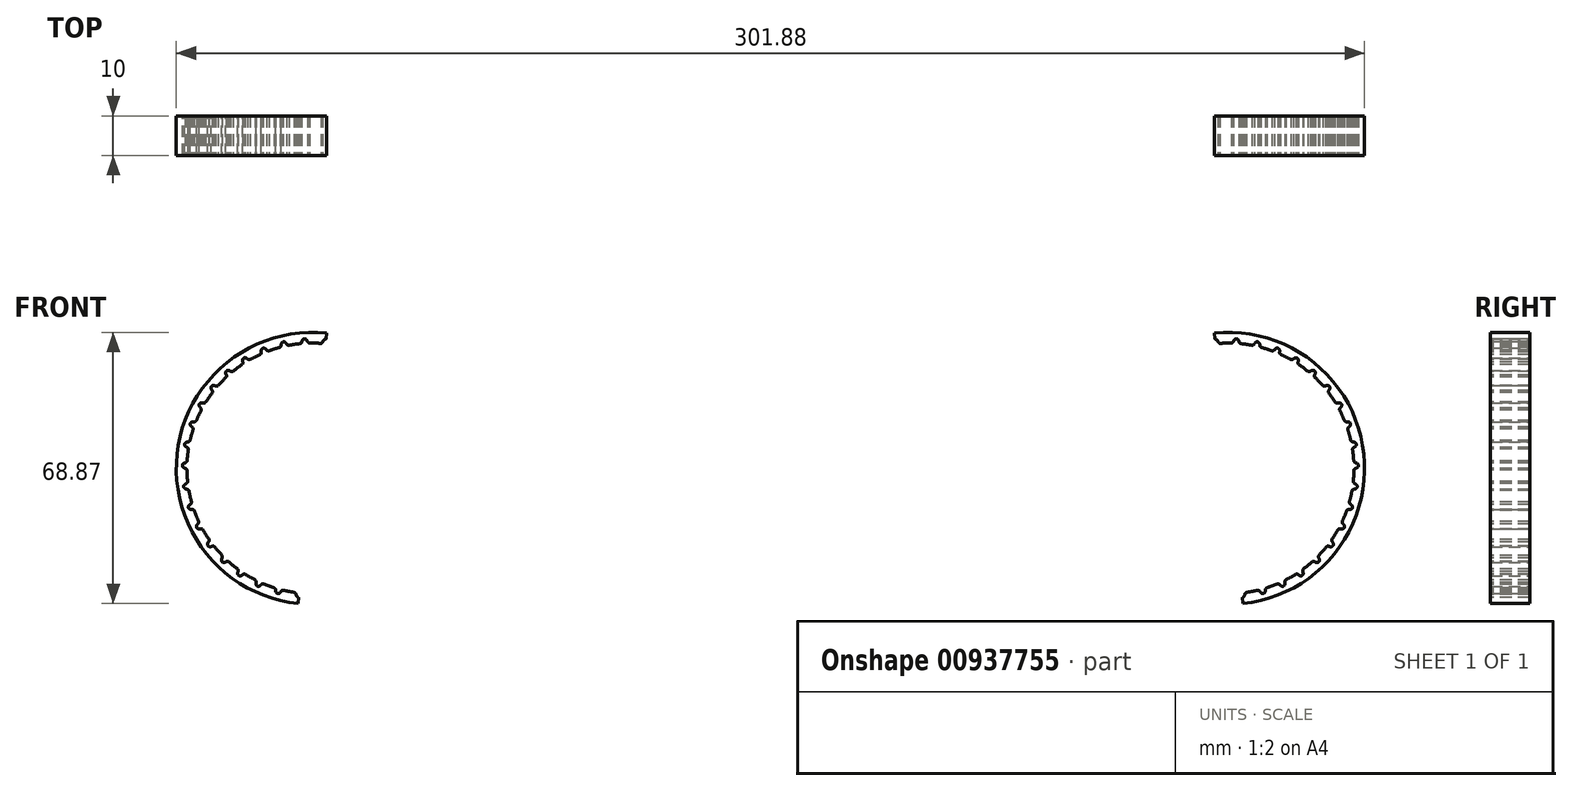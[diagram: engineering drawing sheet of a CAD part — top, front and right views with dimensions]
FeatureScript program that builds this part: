
annotation { "Feature Type Name" : "Feature", "Feature Type Description" : "" }
export const myFeature = defineFeature(function(context is Context, id is Id, definition is map)
    precondition{}
    {
        {
            var Q0;
            Q0=qCreatedBy(makeId("Front.planeOp"),FACE);
            var sketch = newSketch(context, id + "F0", { "sketchPlane" : qUnion([Q0])});
            skArc(sketch, "E0", {"start": v(120.96, -47.24) * mm, "mid": v(122.42, -47) * mm, "end": v(123.87, -46.68) * mm});
            skArc(sketch, "E1", {"start": v(120.05, -50.07) * mm, "mid": v(150.75, -12.1) * mm, "end": v(112.77, 18.6) * mm});
            skEllipticalArc(sketch, "E2.5.0.0", {});
            skArc(sketch, "E2.5.0.1", {"start": v(113.73, 16.4) * mm, "mid": v(113.93, 16.15) * mm, "end": v(114.2, 16) * mm});
            skEllipticalArc(sketch, "E2.5.0.3", {});
            skEllipticalArc(sketch, "E3.1.0", {});
            skArc(sketch, "E3.1.1", {"start": v(119.06, 16.4) * mm, "mid": v(119.2, 16.12) * mm, "end": v(119.46, 15.93) * mm});
            skEllipticalArc(sketch, "E3.2.0", {});
            skArc(sketch, "E3.2.1", {"start": v(124.31, 15.53) * mm, "mid": v(124.41, 15.23) * mm, "end": v(124.63, 15) * mm});
            skEllipticalArc(sketch, "E3.3.0", {});
            skArc(sketch, "E3.3.1", {"start": v(129.35, 13.8) * mm, "mid": v(129.4, 13.49) * mm, "end": v(129.57, 13.23) * mm});
            skEllipticalArc(sketch, "E3.4.0", {});
            skArc(sketch, "E3.4.1", {"start": v(134.04, 11.27) * mm, "mid": v(134.03, 10.95) * mm, "end": v(134.16, 10.67) * mm});
            skEllipticalArc(sketch, "E3.5.0", {});
            skArc(sketch, "E3.5.1", {"start": v(138.24, 8) * mm, "mid": v(138.19, 7.69) * mm, "end": v(138.26, 7.38) * mm});
            skEllipticalArc(sketch, "E3.6.0", {});
            skArc(sketch, "E3.6.1", {"start": v(141.85, 4.08) * mm, "mid": v(141.74, 3.79) * mm, "end": v(141.77, 3.47) * mm});
            skEllipticalArc(sketch, "E3.7.0", {});
            skArc(sketch, "E3.7.1", {"start": v(144.76, -0.37) * mm, "mid": v(144.61, -0.65) * mm, "end": v(144.59, -0.96) * mm});
            skEllipticalArc(sketch, "E3.8.0", {});
            skArc(sketch, "E3.8.1", {"start": v(146.9, -5.25) * mm, "mid": v(146.7, -5.5) * mm, "end": v(146.63, -5.8) * mm});
            skEllipticalArc(sketch, "E3.9.0", {});
            skArc(sketch, "E3.9.1", {"start": v(148.22, -10.41) * mm, "mid": v(147.98, -10.62) * mm, "end": v(147.86, -10.91) * mm});
            skEllipticalArc(sketch, "E3.10.0", {});
            skArc(sketch, "E3.10.1", {"start": v(148.66, -15.72) * mm, "mid": v(148.4, -15.89) * mm, "end": v(148.22, -16.15) * mm});
            skEllipticalArc(sketch, "E3.11.0", {});
            skArc(sketch, "E3.11.1", {"start": v(148.22, -21.03) * mm, "mid": v(147.93, -21.15) * mm, "end": v(147.72, -21.38) * mm});
            skEllipticalArc(sketch, "E3.12.0", {});
            skArc(sketch, "E3.12.1", {"start": v(146.92, -26.19) * mm, "mid": v(146.6, -26.26) * mm, "end": v(146.36, -26.46) * mm});
            skEllipticalArc(sketch, "E3.13.0", {});
            skArc(sketch, "E3.13.1", {"start": v(144.78, -31.07) * mm, "mid": v(144.46, -31.1) * mm, "end": v(144.19, -31.24) * mm});
            skEllipticalArc(sketch, "E3.14.0", {});
            skArc(sketch, "E3.14.1", {"start": v(141.87, -35.53) * mm, "mid": v(141.55, -35.5) * mm, "end": v(141.26, -35.6) * mm});
            skEllipticalArc(sketch, "E3.15.0", {});
            skArc(sketch, "E3.15.1", {"start": v(138.26, -39.45) * mm, "mid": v(137.96, -39.37) * mm, "end": v(137.65, -39.42) * mm});
            skEllipticalArc(sketch, "E3.16.0", {});
            skArc(sketch, "E3.16.1", {"start": v(134.06, -42.72) * mm, "mid": v(133.77, -42.6) * mm, "end": v(133.46, -42.6) * mm});
            skEllipticalArc(sketch, "E3.17.0", {});
            skArc(sketch, "E3.17.1", {"start": v(129.38, -45.26) * mm, "mid": v(129.12, -45.08) * mm, "end": v(128.8, -45.03) * mm});
            skEllipticalArc(sketch, "E3.18.0", {});
            skArc(sketch, "E3.18.1", {"start": v(124.34, -46.99) * mm, "mid": v(124.11, -46.77) * mm, "end": v(123.82, -46.67) * mm});
            skLineSegment(sketch, "E3.anchor1", {"start": v(116.41, -15.73) * mm, "end": v(113.03, 16.09) * mm, "construction": true});
            skArc(sketch, "E4.1.0", {"start": v(117.11, 16.09) * mm, "mid": v(117.42, 16.23) * mm, "end": v(117.64, 16.5) * mm});
            skEllipticalArc(sketch, "E4.1.1", {});
            skArc(sketch, "E4.2.0", {"start": v(122.34, 15.54) * mm, "mid": v(122.67, 15.63) * mm, "end": v(122.93, 15.86) * mm});
            skEllipticalArc(sketch, "E4.2.1", {});
            skArc(sketch, "E4.3.0", {"start": v(127.4, 14.14) * mm, "mid": v(127.75, 14.17) * mm, "end": v(128.04, 14.35) * mm});
            skEllipticalArc(sketch, "E4.3.1", {});
            skArc(sketch, "E4.4.0", {"start": v(132.17, 11.92) * mm, "mid": v(132.52, 11.9) * mm, "end": v(132.83, 12.03) * mm});
            skEllipticalArc(sketch, "E4.4.1", {});
            skArc(sketch, "E4.5.0", {"start": v(136.51, 8.95) * mm, "mid": v(136.84, 8.87) * mm, "end": v(137.18, 8.95) * mm});
            skEllipticalArc(sketch, "E4.5.1", {});
            skArc(sketch, "E4.6.0", {"start": v(140.3, 5.3) * mm, "mid": v(140.62, 5.17) * mm, "end": v(140.96, 5.2) * mm});
            skEllipticalArc(sketch, "E4.6.1", {});
            skArc(sketch, "E4.7.0", {"start": v(143.44, 1.08) * mm, "mid": v(143.73, 0.9) * mm, "end": v(144.07, 0.87) * mm});
            skEllipticalArc(sketch, "E4.7.1", {});
            skArc(sketch, "E4.8.0", {"start": v(145.84, -3.6) * mm, "mid": v(146.1, -3.82) * mm, "end": v(146.42, -3.9) * mm});
            skEllipticalArc(sketch, "E4.8.1", {});
            skArc(sketch, "E4.9.0", {"start": v(147.43, -8.6) * mm, "mid": v(147.65, -8.87) * mm, "end": v(147.96, -9) * mm});
            skEllipticalArc(sketch, "E4.9.1", {});
            skArc(sketch, "E4.10.0", {"start": v(148.18, -13.8) * mm, "mid": v(148.35, -14.1) * mm, "end": v(148.64, -14.3) * mm});
            skEllipticalArc(sketch, "E4.10.1", {});
            skArc(sketch, "E4.11.0", {"start": v(148.07, -19.06) * mm, "mid": v(148.19, -19.38) * mm, "end": v(148.43, -19.62) * mm});
            skEllipticalArc(sketch, "E4.11.1", {});
            skArc(sketch, "E4.12.0", {"start": v(147.09, -24.22) * mm, "mid": v(147.15, -24.56) * mm, "end": v(147.36, -24.83) * mm});
            skEllipticalArc(sketch, "E4.12.1", {});
            skArc(sketch, "E4.13.0", {"start": v(145.27, -29.16) * mm, "mid": v(145.28, -29.5) * mm, "end": v(145.44, -29.8) * mm});
            skEllipticalArc(sketch, "E4.13.1", {});
            skArc(sketch, "E4.14.0", {"start": v(142.67, -33.73) * mm, "mid": v(142.62, -34.06) * mm, "end": v(142.73, -34.39) * mm});
            skEllipticalArc(sketch, "E4.14.1", {});
            skArc(sketch, "E4.15.0", {"start": v(139.35, -37.8) * mm, "mid": v(139.25, -38.13) * mm, "end": v(139.3, -38.47) * mm});
            skEllipticalArc(sketch, "E4.15.1", {});
            skArc(sketch, "E4.16.0", {"start": v(135.4, -41.28) * mm, "mid": v(135.25, -41.58) * mm, "end": v(135.24, -41.92) * mm});
            skEllipticalArc(sketch, "E4.16.1", {});
            skArc(sketch, "E4.17.0", {"start": v(130.94, -44.05) * mm, "mid": v(130.74, -44.33) * mm, "end": v(130.68, -44.66) * mm});
            skEllipticalArc(sketch, "E4.17.1", {});
            skArc(sketch, "E4.18.0", {"start": v(126.08, -46.06) * mm, "mid": v(125.84, -46.3) * mm, "end": v(125.72, -46.62) * mm});
            skEllipticalArc(sketch, "E4.18.1", {});
            skArc(sketch, "E4.19.0", {"start": v(120.96, -47.24) * mm, "mid": v(120.68, -47.43) * mm, "end": v(120.5, -47.73) * mm});
            skEllipticalArc(sketch, "E4.19.1", {});
            skLineSegment(sketch, "E4.anchor2", {"start": v(116.41, -15.73) * mm, "end": v(120.96, -47.24) * mm, "construction": true});
            skPoint(sketch, "E5.orphan", {"position": v(119.1, -47.87) * mm});
            skLineSegment(sketch, "E6", {"start": v(119.8, -47.55) * mm, "end": v(119.77, -47.39) * mm});
            skLineSegment(sketch, "E7", {"start": v(119.89, -48.55) * mm, "end": v(120.05, -50.07) * mm});
            skLineSegment(sketch, "E8", {"start": v(120.05, -50.07) * mm, "end": v(120.06, -50.05) * mm});
            skLineSegment(sketch, "E9", {"start": v(113.05, 15.92) * mm, "end": v(113.03, 16.09) * mm});
            skArc(sketch, "E10.trimOffspring", {"start": v(117.11, 16.09) * mm, "mid": v(115.63, 16.09) * mm, "end": v(114.15, 16.02) * mm});
            skArc(sketch, "E11.trimOffspring", {"start": v(122.34, 15.54) * mm, "mid": v(120.88, 15.78) * mm, "end": v(119.41, 15.95) * mm});
            skArc(sketch, "E12.trimOffspring", {"start": v(127.4, 14.14) * mm, "mid": v(126, 14.62) * mm, "end": v(124.59, 15.03) * mm});
            skArc(sketch, "E13.trimOffspring", {"start": v(132.17, 11.92) * mm, "mid": v(130.87, 12.62) * mm, "end": v(129.54, 13.26) * mm});
            skArc(sketch, "E14.trimOffspring", {"start": v(136.51, 8.95) * mm, "mid": v(135.34, 9.86) * mm, "end": v(134.13, 10.7) * mm});
            skArc(sketch, "E15.trimOffspring", {"start": v(140.3, 5.3) * mm, "mid": v(139.3, 6.4) * mm, "end": v(138.24, 7.43) * mm});
            skArc(sketch, "E16.trimOffspring", {"start": v(143.44, 1.08) * mm, "mid": v(142.63, 2.32) * mm, "end": v(141.76, 3.52) * mm});
            skArc(sketch, "E17.trimOffspring", {"start": v(145.84, -3.6) * mm, "mid": v(145.24, -2.24) * mm, "end": v(144.58, -0.91) * mm});
            skArc(sketch, "E18.trimOffspring", {"start": v(147.43, -8.6) * mm, "mid": v(147.07, -7.17) * mm, "end": v(146.64, -5.75) * mm});
            skArc(sketch, "E19.trimOffspring", {"start": v(148.18, -13.8) * mm, "mid": v(148.06, -12.33) * mm, "end": v(147.87, -10.86) * mm});
            skArc(sketch, "E20.trimOffspring", {"start": v(148.07, -19.06) * mm, "mid": v(148.19, -17.58) * mm, "end": v(148.24, -16.1) * mm});
            skArc(sketch, "E21.trimOffspring", {"start": v(147.09, -24.22) * mm, "mid": v(147.45, -22.79) * mm, "end": v(147.75, -21.34) * mm});
            skArc(sketch, "E22.trimOffspring", {"start": v(145.27, -29.16) * mm, "mid": v(145.87, -27.8) * mm, "end": v(146.4, -26.42) * mm});
            skArc(sketch, "E23.trimOffspring", {"start": v(142.67, -33.73) * mm, "mid": v(143.48, -32.49) * mm, "end": v(144.23, -31.2) * mm});
            skArc(sketch, "E24.trimOffspring", {"start": v(139.35, -37.8) * mm, "mid": v(140.35, -36.71) * mm, "end": v(141.3, -35.58) * mm});
            skArc(sketch, "E25.trimOffspring", {"start": v(135.4, -41.28) * mm, "mid": v(136.57, -40.37) * mm, "end": v(137.7, -39.4) * mm});
            skArc(sketch, "E26.trimOffspring", {"start": v(130.94, -44.05) * mm, "mid": v(132.24, -43.35) * mm, "end": v(133.51, -42.58) * mm});
            skArc(sketch, "E27.trimOffspring", {"start": v(126.08, -46.06) * mm, "mid": v(127.48, -45.58) * mm, "end": v(128.86, -45.03) * mm});
            skLineSegment(sketch, "E28.trimOffspring", {"start": v(112.93, 17.08) * mm, "end": v(112.77, 18.6) * mm});
            const initialGuessF0  = {"E2.5.0.0": [0.11303482814067517, 0.016085284111386752, -0.09793029370573542, 0.9951932764919127, 0.001, 0.0007199110732306023, 0, 0.010662289715557305], "E2.5.0.3": [0.11303482814067461, 0.016085284111387186, -0.09793029370571554, 0.9951932764919146, 0.001, 0.00075, 4.958959793330978, 6.283185307179577], "E3.1.0": [0.11831822491139382, 0.01620729971119933, 0.06720877745214683, 0.997738933906755, 0.001, 0.00075, 4.958959793330976, 0], "E3.2.0": [0.12354964614421307, 0.01545803265049844, 0.23051456836132156, 0.9730688741159045, 0.001, 0.00075, 4.958959793330976, 0], "E3.3.0": [0.12858639230519847, 0.013857920981506955, 0.38753252275223143, 0.921856032040411, 0.001, 0.00075, 4.958959793330976, 0], "E3.4.0": [0.13329107408889557, 0.011450611579375158, 0.5339796001443508, 0.8454973605101789, 0.001, 0.00075, 4.958959793330976, 0], "E3.5.0": [0.13753536004043526, 0.008301769569205947, 0.6658611060254611, 0.746075725032352, 0.001, 0.00075, 4.958959793330976, 0], "E3.6.0": [0.14120347710308728, 0.00449728715261824, 0.7795796567045535, 0.6263030886499048, 0.001, 0.00075, 4.958959793330976, 0], "E3.7.0": [0.14419536860544996, 0.00014094069239109497, 0.8720333065612396, 0.4894465366593897, 0.001, 0.00075, 4.958959793330976, 0], "E3.8.0": [0.14642942354661792, -0.004648440036188195, 0.9407001610361064, 0.3392391590407031, 0.001, 0.00075, 4.958959793330976, 0], "E3.9.0": [0.14784470273154268, -0.00974021321182772, 0.98370716734021, 0.179778221493873, 0.001, 0.00075, 4.958959793330976, 0], "E3.10.0": [0.14840260103341701, -0.014995488535558099, 0.9998812064524727, 0.0154134027115367, 0.001, 0.00075, 4.958959793330976, 0], "E3.11.0": [0.1480879004408981, -0.02027091579602827, 0.9887810927484848, -0.14937185351702803, 0.001, 0.00075, 4.958959793330976, 0], "E3.12.0": [0.14690918516578663, -0.025422595089585068, 0.9507096083942551, -0.3100826349650073, 0.001, 0.00075, 4.9589597933309575, 6.283185307179583], "E3.13.0": [0.14489860748810623, -0.030310002034525982, 0.8867052442380137, -0.46233517045624434, 0.001, 0.00075, 4.958959793330978, 6.283185307179582], "E3.14.0": [0.14211101072571924, -0.034799820909912065, 0.7985138724870178, -0.6019764077152749, 0.001, 0.00075, 4.958959793330948, 0], "E3.15.0": [0.13862243325158113, -0.03876958116090705, 0.6885411238648864, -0.72519729780721, 0.001, 0.00075, 4.9589597933309735, 6.283185307179575], "E3.16.0": [0.1345280343651436, -0.04211099807625639, 0.5597867682764718, -0.8286366960632288, 0.001, 0.00075, 4.958959793330938, 0], "E3.17.0": [0.12993949859472742, -0.044732926512933195, 0.4157628889046707, -0.9094730453452936, 0.001, 0.00075, 4.958959793330925, 6.283185307179573], "E3.18.0": [0.12498198923472943, -0.046563847098042246, 0.26039808173651235, -0.9655013407696256, 0.001, 0.00075, 4.958959793330958, 0], "E4.1.1": [0.11831822491139428, 0.016207299711198813, 0.0672087774521269, 0.9977389339067563, 0.001, 0.0007199110732306023, 0, 1.3242255138486463], "E4.2.1": [0.12354964614421346, 0.015458032650497847, 0.23051456836130213, 0.973068874115909, 0.001, 0.0007199110732306023, 0, 1.3242255138486463], "E4.3.1": [0.12858639230519875, 0.01385792098150631, 0.38753252275221306, 0.9218560320404188, 0.001, 0.0007199110732306023, 0, 1.3242255138486463], "E4.4.1": [0.13329107408889576, 0.011450611579374478, 0.5339796001443338, 0.8454973605101896, 0.001, 0.0007199110732306023, 0, 1.3242255138486463], "E4.5.1": [0.13753536004043532, 0.008301769569205253, 0.6658611060254462, 0.7460757250323654, 0.001, 0.0007199110732306023, 0, 1.3242255138486463], "E4.6.1": [0.14120347710308723, 0.004497287152617546, 0.7795796567045411, 0.6263030886499203, 0.001, 0.0007199110732306023, 0, 1.3242255138486463], "E4.7.1": [0.1441953686054498, 0.00014094069239041496, 0.8720333065612298, 0.4894465366594071, 0.001, 0.0007199110732306023, 0, 1.3242255138486463], "E4.8.1": [0.14642942354661762, -0.004648440036188847, 0.9407001610360997, 0.33923915904072194, 0.001, 0.0007199110732306023, 0, 1.3242255138486463], "E4.9.1": [0.1478447027315423, -0.009740213211828302, 0.9837071673402066, 0.17977822149389266, 0.001, 0.0007199110732306023, 0, 1.3242255138486463], "E4.10.1": [0.14840260103341651, -0.014995488535558626, 0.9998812064524724, 0.015413402711556654, 0.001, 0.0007199110732306023, 0, 1.3242255138486463], "E4.11.1": [0.14808790044089754, -0.020270915796028702, 0.9887810927484878, -0.14937185351700832, 0.001, 0.0007199110732306023, 0, 1.3242255138486463], "E4.12.1": [0.146909185165786, -0.02542259508958547, 0.9507096083942608, -0.3100826349649908, 0.001, 0.0007199110732306023, 0, 1.3242255138486463], "E4.13.1": [0.14489860748810554, -0.030310002034526315, 0.8867052442380217, -0.46233517045622935, 0.001, 0.0007199110732306023, 0, 1.3242255138486463], "E4.14.1": [0.1421110107257185, -0.03479982090991225, 0.7985138724870282, -0.6019764077152611, 0.001, 0.0007199110732306023, 0, 1.3242255138486463], "E4.15.1": [0.13862243325158036, -0.0387695811609071, 0.6885411238648989, -0.7251972978071982, 0.001, 0.0007199110732306023, 0, 1.3242255138486463], "E4.16.1": [0.13452803436514282, -0.042110998076256324, 0.5597867682764859, -0.8286366960632193, 0.001, 0.0007199110732306023, 0, 1.3242255138486463], "E4.17.1": [0.1299394985947266, -0.04473292651293303, 0.41576288890468527, -0.9094730453452871, 0.001, 0.0007199110732306023, 0, 1.3242255138486463], "E4.18.1": [0.1249819892347287, -0.04656384709804196, 0.26039808173652823, -0.9655013407696214, 0.001, 0.0007199110732306023, 0, 1.3242255138486463], "E4.19.1": [0.11979073421722736, -0.047553817090875125, 0.09793029370573554, -0.9951932764919127, 0.001, 0.0007199110732306023, 0, 1.3242255138486463]};
            skSetInitialGuess(sketch, initialGuessF0);
            skSolve(sketch);
        }
        {
            var Q0;
            {var subQ2=sQuery(id+"F0.wireOp",EDGE,"E3.6.0");Q0=makeQuery(id+"F0.imprint","IMPRINT",FACE,{"disambiguationData":[TD([[makeQuery(id+"F0.imprint","IMPRINT",EDGE,{"derivedFrom":subQ2}),1.0]])]});}
            var Q1;
            {var subQ44=sQuery(id+"F0.wireOp",EDGE,"E1");Q1=makeQuery(id+"F0.imprint","IMPRINT",FACE,{"disambiguationData":[TD([[makeQuery(id+"F0.imprint","IMPRINT",EDGE,{"derivedFrom":subQ44}),1.0]])]});}
            extrude(context, id + "F1", {"entities" : qUnion([Q0, Q1]), "oppositeDirection" : true, "depth" : 10 * mm, "offsetDistance" : 25 * mm});
        }
        {
            var Q0;
            Q0=makeQuery(id+"F1.opExtrude","SWEPT_BODY",BODY,{"disambiguationData":[OSD([sQuery(id+"F0.wireOp",EDGE,"E0"),sQuery(id+"F0.wireOp",EDGE,"E1"),sQuery(id+"F0.wireOp",EDGE,"E2.5.0.0"),sQuery(id+"F0.wireOp",EDGE,"E2.5.0.1"),sQuery(id+"F0.wireOp",EDGE,"E2.5.0.3"),sQuery(id+"F0.wireOp",EDGE,"E3.1.0"),sQuery(id+"F0.wireOp",EDGE,"E3.1.1"),sQuery(id+"F0.wireOp",EDGE,"E3.2.0"),sQuery(id+"F0.wireOp",EDGE,"E3.2.1"),sQuery(id+"F0.wireOp",EDGE,"E3.3.0"),sQuery(id+"F0.wireOp",EDGE,"E3.3.1"),sQuery(id+"F0.wireOp",EDGE,"E3.4.0"),sQuery(id+"F0.wireOp",EDGE,"E3.4.1"),sQuery(id+"F0.wireOp",EDGE,"E3.5.0"),sQuery(id+"F0.wireOp",EDGE,"E3.5.1"),sQuery(id+"F0.wireOp",EDGE,"E3.6.0"),sQuery(id+"F0.wireOp",EDGE,"E3.6.1"),sQuery(id+"F0.wireOp",EDGE,"E3.7.0"),sQuery(id+"F0.wireOp",EDGE,"E3.7.1"),sQuery(id+"F0.wireOp",EDGE,"E3.8.0"),sQuery(id+"F0.wireOp",EDGE,"E3.8.1"),sQuery(id+"F0.wireOp",EDGE,"E3.9.0"),sQuery(id+"F0.wireOp",EDGE,"E3.9.1"),sQuery(id+"F0.wireOp",EDGE,"E3.10.0"),sQuery(id+"F0.wireOp",EDGE,"E3.10.1"),sQuery(id+"F0.wireOp",EDGE,"E3.11.0"),sQuery(id+"F0.wireOp",EDGE,"E3.11.1"),sQuery(id+"F0.wireOp",EDGE,"E3.12.0"),sQuery(id+"F0.wireOp",EDGE,"E3.12.1"),sQuery(id+"F0.wireOp",EDGE,"E3.13.0"),sQuery(id+"F0.wireOp",EDGE,"E3.13.1"),sQuery(id+"F0.wireOp",EDGE,"E3.14.0"),sQuery(id+"F0.wireOp",EDGE,"E3.14.1"),sQuery(id+"F0.wireOp",EDGE,"E3.15.0"),sQuery(id+"F0.wireOp",EDGE,"E3.15.1"),sQuery(id+"F0.wireOp",EDGE,"E3.16.0"),sQuery(id+"F0.wireOp",EDGE,"E3.16.1"),sQuery(id+"F0.wireOp",EDGE,"E3.17.0"),sQuery(id+"F0.wireOp",EDGE,"E3.17.1"),sQuery(id+"F0.wireOp",EDGE,"E3.18.0"),sQuery(id+"F0.wireOp",EDGE,"E3.18.1"),sQuery(id+"F0.wireOp",EDGE,"E4.1.0"),sQuery(id+"F0.wireOp",EDGE,"E4.1.1"),sQuery(id+"F0.wireOp",EDGE,"E4.2.0"),sQuery(id+"F0.wireOp",EDGE,"E4.2.1"),sQuery(id+"F0.wireOp",EDGE,"E4.3.0"),sQuery(id+"F0.wireOp",EDGE,"E4.3.1"),sQuery(id+"F0.wireOp",EDGE,"E4.4.0"),sQuery(id+"F0.wireOp",EDGE,"E4.4.1"),sQuery(id+"F0.wireOp",EDGE,"E4.5.0"),sQuery(id+"F0.wireOp",EDGE,"E4.5.1"),sQuery(id+"F0.wireOp",EDGE,"E4.6.0"),sQuery(id+"F0.wireOp",EDGE,"E4.6.1"),sQuery(id+"F0.wireOp",EDGE,"E4.7.0"),sQuery(id+"F0.wireOp",EDGE,"E4.7.1"),sQuery(id+"F0.wireOp",EDGE,"E4.8.0"),sQuery(id+"F0.wireOp",EDGE,"E4.8.1"),sQuery(id+"F0.wireOp",EDGE,"E4.9.0"),sQuery(id+"F0.wireOp",EDGE,"E4.9.1"),sQuery(id+"F0.wireOp",EDGE,"E4.10.0"),sQuery(id+"F0.wireOp",EDGE,"E4.10.1"),sQuery(id+"F0.wireOp",EDGE,"E4.11.0"),sQuery(id+"F0.wireOp",EDGE,"E4.11.1"),sQuery(id+"F0.wireOp",EDGE,"E4.12.0"),sQuery(id+"F0.wireOp",EDGE,"E4.12.1"),sQuery(id+"F0.wireOp",EDGE,"E4.13.0"),sQuery(id+"F0.wireOp",EDGE,"E4.13.1"),sQuery(id+"F0.wireOp",EDGE,"E4.14.0"),sQuery(id+"F0.wireOp",EDGE,"E4.14.1"),sQuery(id+"F0.wireOp",EDGE,"E4.15.0"),sQuery(id+"F0.wireOp",EDGE,"E4.15.1"),sQuery(id+"F0.wireOp",EDGE,"E4.16.0"),sQuery(id+"F0.wireOp",EDGE,"E4.16.1"),sQuery(id+"F0.wireOp",EDGE,"E4.17.0"),sQuery(id+"F0.wireOp",EDGE,"E4.17.1"),sQuery(id+"F0.wireOp",EDGE,"E4.18.0"),sQuery(id+"F0.wireOp",EDGE,"E4.18.1"),sQuery(id+"F0.wireOp",EDGE,"E4.19.0"),sQuery(id+"F0.wireOp",EDGE,"E4.19.1"),sQuery(id+"F0.wireOp",EDGE,"E7"),sQuery(id+"F0.wireOp",EDGE,"E10.trimOffspring"),sQuery(id+"F0.wireOp",EDGE,"E11.trimOffspring"),sQuery(id+"F0.wireOp",EDGE,"E12.trimOffspring"),sQuery(id+"F0.wireOp",EDGE,"E13.trimOffspring"),sQuery(id+"F0.wireOp",EDGE,"E14.trimOffspring"),sQuery(id+"F0.wireOp",EDGE,"E15.trimOffspring"),sQuery(id+"F0.wireOp",EDGE,"E16.trimOffspring"),sQuery(id+"F0.wireOp",EDGE,"E17.trimOffspring"),sQuery(id+"F0.wireOp",EDGE,"E18.trimOffspring"),sQuery(id+"F0.wireOp",EDGE,"E19.trimOffspring"),sQuery(id+"F0.wireOp",EDGE,"E20.trimOffspring"),sQuery(id+"F0.wireOp",EDGE,"E21.trimOffspring"),sQuery(id+"F0.wireOp",EDGE,"E22.trimOffspring"),sQuery(id+"F0.wireOp",EDGE,"E23.trimOffspring"),sQuery(id+"F0.wireOp",EDGE,"E24.trimOffspring"),sQuery(id+"F0.wireOp",EDGE,"E25.trimOffspring"),sQuery(id+"F0.wireOp",EDGE,"E26.trimOffspring"),sQuery(id+"F0.wireOp",EDGE,"E27.trimOffspring"),sQuery(id+"F0.wireOp",EDGE,"E28.trimOffspring")])]});
            var Q1;
            Q1=qCreatedBy(makeId("Right.planeOp"),FACE);
            mirror(context, id + "F2", {"entities" : qUnion([Q0]), "mirrorPlane" : qUnion([Q1])});
        }
    });
